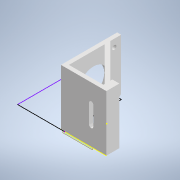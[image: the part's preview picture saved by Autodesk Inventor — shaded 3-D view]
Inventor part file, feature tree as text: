
AUTODESK INVENTOR PART (.ipt)
format: ipt  version: 2022.2 (Build 262287000, 287)  size: 276,992 bytes
history: native  units: mm
features: sketch x8, reference x8, extrude x7, other x6, projected_geometry x5, plane x4, fillet x1
ambient origin geometry x8: Origin, YZ Plane, XZ Plane, XY Plane, X Axis, Y Axis, Z Axis, Center Point
bodies: Solid1 (feature_tree)
feature tree (39):
  extrude  "Extrusion1"  Depth=3.0mm
  sketch  "Sketch5"  dims[d3=3.0mm d4=10.0mm d5=0.0mm]
  plane  "Work Plane1"
  extrude  "Extrusion2"  Depth=10.0mm TaperAngle=0.0deg
  extrude  "Extrusion7"  Depth=10.0mm
  plane  "Work Plane6"
  extrude  "Extrusion3"  Depth=1.59mm
  plane  "Work Plane5"
  extrude  "Extrusion5"  Depth=10.0mm
  plane  "Work Plane3"
  sketch  "Sketch14"  dims[d25=3.0mm d26=45.0deg]
  extrude  "Extrusion9"  TaperAngle=45.0deg  [1 undecoded]
  extrude  "Extrusion10"  TaperAngle=0.0deg  [1 undecoded]
  fillet  "Fillet3"  Radius=2.0mm
  sketch  "Sketch2"  dims[d0=3.0mm d1=0.0mm d2=5.0mm]
  reference  "Reference2"
  reference  "Reference3"
  sketch  "Sketch7"  dims[d11=10.0mm d12=0.0mm d16=4.59mm]
  projected_geometry  "Projected Loop1"
  sketch  "Sketch10"  dims[d17=4.59mm d18=1.59mm]
  reference  "Reference8"
  reference  "Reference9"
  reference  "Reference10"
  reference  "Reference11"
  sketch  "Sketch12"  dims[d19=10.0mm d20=0.0mm d23=2.5mm]
  projected_geometry  "Projected Loop2"
  sketch  "Sketch15"  dims[d27=2.0mm d28=0.0mm d31=0.0mm d32=0.0mm d33=2.0mm d34=0.0mm]
  reference  "Reference12"
  reference  "Reference13"
  projected_geometry  "Projected Loop5"
  sketch  "Sketch16"  dims[d35=2.0mm d24=0.5mm]
  projected_geometry  "Projected Loop6"
  projected_geometry  "Projected Loop7"
  other  "<userpath>\Documents\Inventor\Wire Bender\Assembly.iam"
  other  "Assembly.iam"
  other  "17HM15-0904S:1"
  other  "nema17_top_40mm___ __________4"
  other  "Feed Motor Mount:1"
  other  "Tool Head:1"
note: 2 required parameter values undecoded (feature->parameter linkage not recoverable at this tier; creation-order binding heuristic only, values carry confidence <= 0.55)
